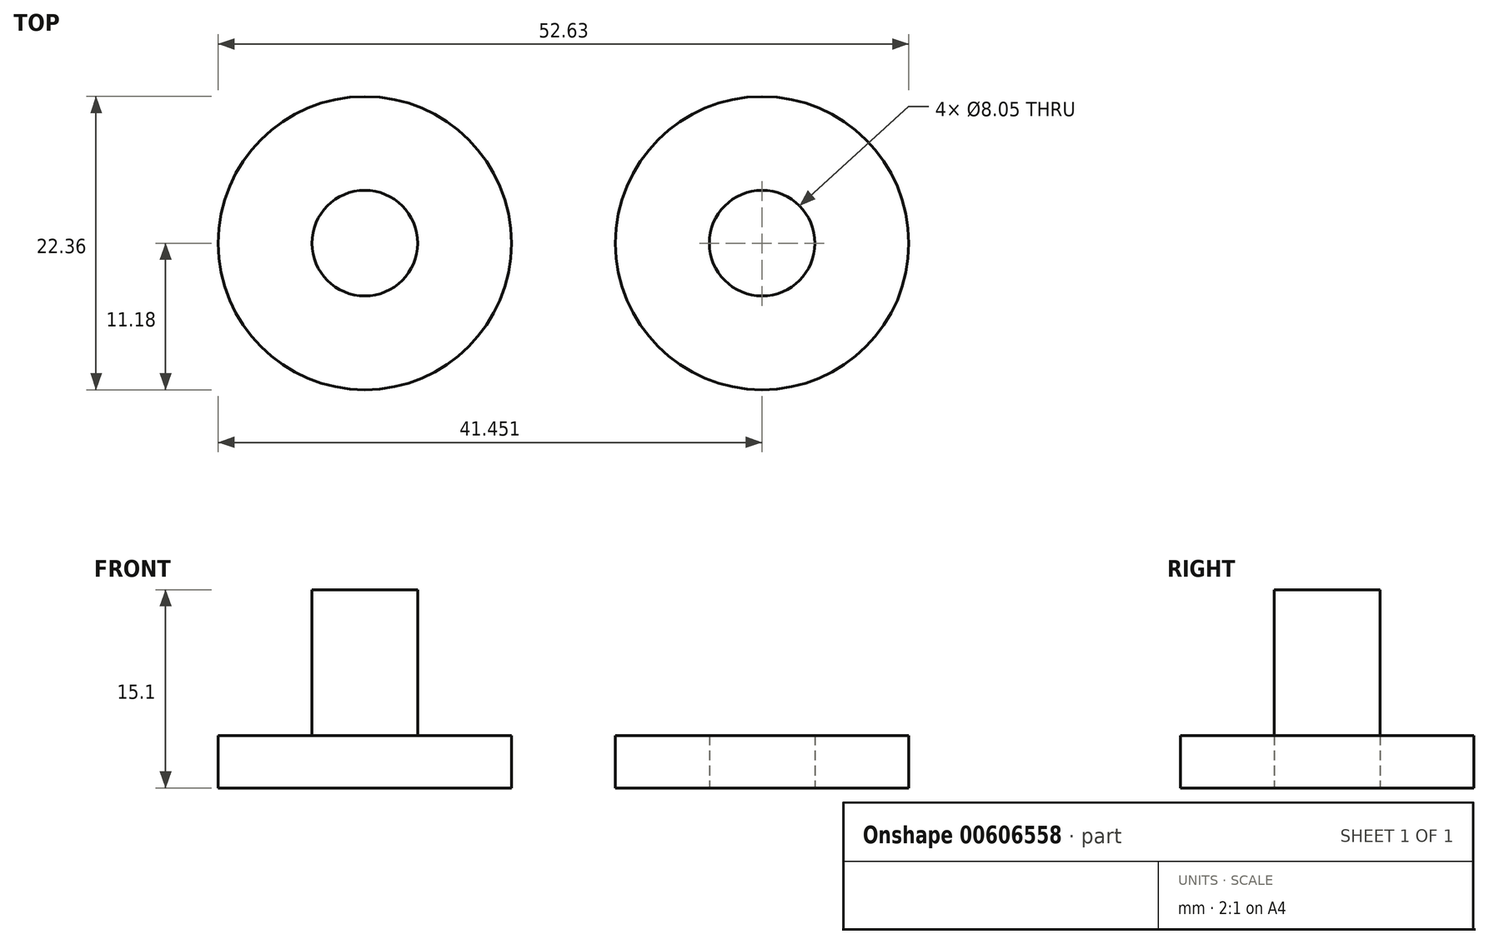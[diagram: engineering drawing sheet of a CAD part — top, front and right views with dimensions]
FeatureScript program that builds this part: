
annotation { "Feature Type Name" : "Feature", "Feature Type Description" : "" }
export const myFeature = defineFeature(function(context is Context, id is Id, definition is map)
    precondition{}
    {
        {
            var Q0;
            Q0=qCreatedBy(makeId("Top.planeOp"),FACE);
            var sketch = newSketch(context, id + "F0", { "sketchPlane" : qUnion([Q0])});
            skCircle(sketch, "E0", {"center": v(0, 0) * mm, "radius": 11.18 * mm});
            skCircle(sketch, "E1", {"center": v(0, 0) * mm, "radius": 4.03 * mm});
            skCircle(sketch, "E2", {"center": v(30.27, 0) * mm, "radius": 11.18 * mm});
            skCircle(sketch, "E3", {"center": v(30.27, 0) * mm, "radius": 4.03 * mm});
            skSolve(sketch);
        }
        {
            var Q0;
            Q0=makeQuery(id+"F0.imprint","IMPRINT",FACE,{"disambiguationData":[TD([[makeQuery(id+"F0.imprint","IMPRINT",EDGE,{"derivedFrom":sQuery(id+"F0.wireOp",EDGE,"E0")}),1.0]])]});
            extrude(context, id + "F1", {"entities" : qUnion([Q0]), "depth" : 4 * mm, "offsetDistance" : 25 * mm});
        }
        {
            var Q0;
            Q0=makeQuery(id+"F0.imprint","IMPRINT",FACE,{"disambiguationData":[TD([[makeQuery(id+"F0.imprint","IMPRINT",EDGE,{"derivedFrom":sQuery(id+"F0.wireOp",EDGE,"E2")}),1.0]])]});
            extrude(context, id + "F2", {"entities" : qUnion([Q0]), "depth" : 4 * mm, "offsetDistance" : 25 * mm});
        }
        {
            var Q0;
            Q0=makeQuery(id+"F0.imprint","IMPRINT",FACE,{"disambiguationData":[TD([[makeQuery(id+"F0.imprint","IMPRINT",EDGE,{"derivedFrom":sQuery(id+"F0.wireOp",EDGE,"E1")}),1.0]])]});
            extrude(context, id + "F3", {"entities" : qUnion([Q0]), "operationType" : NewBodyOperationType.ADD, "depth" : 15.1 * mm, "offsetDistance" : 25 * mm});
        }
    });
